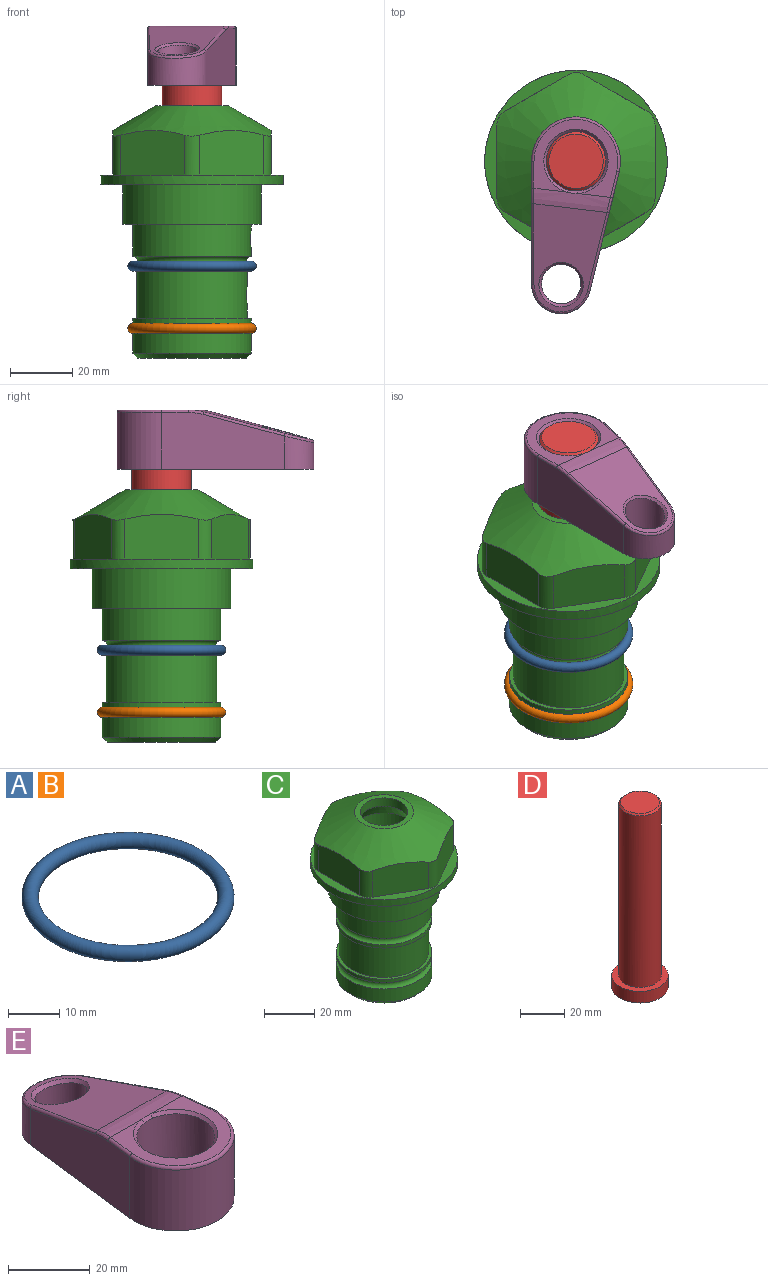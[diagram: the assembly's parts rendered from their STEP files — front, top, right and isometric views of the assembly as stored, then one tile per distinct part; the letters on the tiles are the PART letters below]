
ASSEMBLY  parts=5 mates=4
PART A: 1 faces, bbox 44.7x44.7x3.2 mm
  f0: torus R=19.05mm, axis (0,0,1), area 1193.9mm2
PART B: same geometry as A
PART C: 36 faces, bbox 58.7x58.7x81 mm
  f0: cylinder r=17.78mm len=35.56mm, axis (0,0,1), area 1670.8mm2, adj f23,f24,f31
  f1: cylinder r=19.05mm len=38.1mm, axis (0,0,1), area 1191.9mm2, adj f26,f27,f30
  f2: plane 58.66x58.66mm, normal (0,0,-1), area 1150.6mm2, adj f3,f28
  f3: cylinder r=29.33mm len=58.66mm, axis (0,0,-1), area 585.1mm2, adj f2,f4
  f4: plane 58.66x58.66mm, normal (0,0,1), area 475.9mm2, adj f3,f5,f6,f7,f8,f9,f10,f11
  f5: plane 20.32x14.34mm, normal (-0.5,0.87,0), area 324.4mm2, adj f4,f15,f16,f17
  f6: plane 20.32x14.34mm, normal (0.5,0.87,0), area 324.4mm2, adj f4,f14,f15,f17
  f7: plane 23.48x14.34mm, normal (1,0,0), area 324.4mm2, adj f4,f13,f14,f17
  f8: plane 20.32x14.34mm, normal (0.5,-0.87,0), area 324.4mm2, adj f4,f12,f13,f17
  f9: plane 20.32x14.34mm, normal (-0.5,-0.87,0), area 324.4mm2, adj f4,f11,f12,f17
  f10: plane 23.48x14.34mm, normal (-1,0,0), area 324.4mm2, adj f4,f11,f16,f17
  f11: cylinder r=5.08mm len=12.85mm, axis (0,0,-1), area 67.2mm2, adj f4,f9,f10,f17
  f12: cylinder r=5.08mm len=12.85mm, axis (0,0,-1), area 67.2mm2, adj f4,f8,f9,f17
  f13: cylinder r=5.08mm len=12.85mm, axis (0,0,-1), area 67.2mm2, adj f4,f7,f8,f17
  f14: cylinder r=5.08mm len=12.85mm, axis (0,0,-1), area 67.2mm2, adj f4,f6,f7,f17
  f15: cylinder r=5.08mm len=12.85mm, axis (0,0,-1), area 67.2mm2, adj f4,f5,f6,f17
  f16: cylinder r=5.08mm len=12.85mm, axis (0,0,-1), area 67.2mm2, adj f4,f5,f10,f17
  f17: cone r=11.73mm half-angle=60deg, axis (0,0,-1), area 2071.8mm2, adj f5,f6,f7,f8,f9,f10,f11,f12
  f18: plane 23.46x23.46mm, normal (0,0,1), area 147.4mm2, adj f17,f35
  f19: plane 34.93x34.93mm, normal (0,0,-1), area 958mm2, adj f29
  f20: cylinder r=19.05mm len=38.1mm, axis (0,0,1), area 760.1mm2, adj f21,f29
  f21: torus R=19.05mm, axis (0,0,1), area 565.3mm2, adj f20,f22
  f22: cylinder r=19.05mm len=38.1mm, axis (0,0,1), area 190mm2, adj f21,f23
  f23: plane 38.1x38.1mm, normal (0,0,1), area 146.9mm2, adj f0,f22
  f24: plane 38.1x38.1mm, normal (0,0,-1), area 146.9mm2, adj f0,f25
  f25: cylinder r=19.05mm len=38.1mm, axis (0,0,1), area 190mm2, adj f24,f26
  f26: torus R=19.05mm, axis (0,0,1), area 565.3mm2, adj f1,f25
  f27: plane 44.45x44.45mm, normal (0,0,-1), area 411.7mm2, adj f1,f28
  f28: cylinder r=22.23mm len=44.45mm, axis (0,0,1), area 1773.5mm2, adj f2,f27
  f29: cone r=19.05mm half-angle=45deg, axis (0,0,1), area 257.5mm2, adj f19,f20
  f30: cylinder r=3.17mm len=6.75mm, axis (-1,0,0), area 128mm2, adj f1,f33
  f31: cylinder r=3.17mm len=6.35mm, axis (-1,0,0), area 102.5mm2, adj f0,f33
  f32: plane 25.4x25.4mm, normal (0,0,1), area 506.7mm2, adj f33
  f33: cylinder r=12.7mm len=66.42mm, axis (0,0,-1), area 5236.2mm2, adj f30,f31,f32,f34
  f34: cone r=9.53mm half-angle=30deg, axis (0,0,-1), area 443.4mm2, adj f33,f35
  f35: cylinder r=9.53mm len=19.05mm, axis (0,0,-1), area 240.9mm2, adj f18,f34
PART D: 6 faces, bbox 25.4x25.4x101.6 mm
  f0: plane 17.46x17.46mm, normal (0,0,1), area 239.5mm2, adj f5
  f1: plane 25.4x25.4mm, normal (0,0,-1), area 506.7mm2, adj f2
  f2: cylinder r=12.7mm len=25.4mm, axis (0,0,1), area 506.7mm2, adj f1,f3
  f3: plane 25.4x25.4mm, normal (0,0,1), area 221.7mm2, adj f2,f4
  f4: cylinder r=9.53mm len=94.46mm, axis (0,0,1), area 5653mm2, adj f3,f5
  f5: cone r=8.73mm half-angle=45deg, axis (0,0,-1), area 64.4mm2, adj f0,f4
PART E: 31 faces, bbox 31.7x65.5x19.8 mm
  f0: plane 39.12x18.26mm, normal (0.99,0.12,0), area 612.2mm2, adj f1,f4,f7,f11,f13,f15
  f1: cylinder r=9.53mm len=18.91mm, axis (0,0,-1), area 296.1mm2, adj f0,f2,f7,f17
  f2: plane 39.12x18.26mm, normal (-0.99,0.12,0), area 612.2mm2, adj f1,f4,f7,f12,f14,f16
  f3: cylinder r=6.35mm len=12.7mm, axis (0,0,-1), area 362.4mm2, adj f7,f18
  f4: cylinder r=14.29mm len=28.58mm, axis (0,0,-1), area 882.2mm2, adj f0,f2,f7,f10
  f5: cylinder r=9.53mm len=19.05mm, axis (0,0,-1), area 1092.6mm2, adj f7,f19,f20
  f6: plane 26.99x23.69mm, normal (0,0,1), area 216.2mm2, adj f9,f10,f11,f12,f19
  f7: plane 63.5x28.58mm, normal (0,0,-1), area 661.8mm2, adj f0,f1,f2,f3,f4,f5,f22,f23
  f8: plane 33.52x23.6mm, normal (0,0.26,0.97), area 486mm2, adj f9,f15,f16,f17,f18
  f9: cylinder r=19.05mm len=24.72mm, axis (1,0,0), area 120.4mm2, adj f6,f8,f13,f14,f20
  f10: torus R=13.49mm, axis (0,0,1), area 59mm2, adj f4,f6,f11,f12
  f11: cylinder r=0.79mm len=8.67mm, axis (0.12,-0.99,0), area 10.8mm2, adj f0,f6,f10,f13
  f12: cylinder r=0.79mm len=8.67mm, axis (0.12,0.99,0), area 10.8mm2, adj f2,f6,f10,f14
  f13: bspline ~4.95x1.42mm, area 6.1mm2, adj f0,f9,f11,f15
  f14: bspline ~4.95x1.42mm, area 6.1mm2, adj f2,f9,f12,f16
  f15: cylinder r=0.79mm len=25.95mm, axis (0.12,-0.96,0.26), area 32.9mm2, adj f0,f8,f13,f17
  f16: cylinder r=0.79mm len=25.95mm, axis (0.12,0.96,-0.26), area 32.9mm2, adj f2,f8,f14,f17
  f17: bspline ~18.91x8.38mm, area 30mm2, adj f1,f8,f15,f16
  f18: bspline ~14.29x14.29mm, area 48.3mm2, adj f3,f8
  f19: cone r=9.53mm half-angle=45deg, axis (0,0,1), area 66.5mm2, adj f5,f6,f20
  f20: bspline ~3.22x0.96mm, area 3.5mm2, adj f5,f9,f19
  f21: plane 2.75x2.72mm, normal (0,0,-1), area 2.9mm2, adj f23,f25,f28
  f22: plane 23.05x15.88mm, normal (-0.99,-0.12,0), area 323.6mm2, adj f7,f25,f26,f27,f28,f29
  f23: plane 23.05x15.88mm, normal (0.99,-0.12,0), area 323.6mm2, adj f7,f21,f25,f27,f28,f30
  f24: cylinder r=9.53mm len=10.69mm, axis (0,0,-1), area 114.7mm2, adj f7,f27,f29,f30
  f25: cylinder r=12.7mm len=20.59mm, axis (0,0,-1), area 381.1mm2, adj f7,f21,f22,f23,f26,f28
  f26: plane 2.75x2.72mm, normal (0,0,-1), area 2.9mm2, adj f22,f25,f28
  f27: plane 19.72x18.37mm, normal (0,-0.26,-0.97), area 291.8mm2, adj f22,f23,f24,f28,f29,f30
  f28: cylinder r=15.88mm len=19.92mm, axis (1,0,0), area 54.8mm2, adj f21,f22,f23,f25,f26,f27
  f29: cylinder r=1.59mm len=11mm, axis (0,0,-1), area 34.7mm2, adj f7,f22,f24,f27
  f30: cylinder r=1.59mm len=11mm, axis (0,0,-1), area 34.7mm2, adj f7,f23,f24,f27
PLACE A t=(0,0,-1.59)mm
PLACE B t=(0,0,-21.59)mm
PLACE C at identity fixed
PLACE D rot(axis=(0,0,1),173.1deg) t=(0,0,-12.45)mm
PLACE E rot(axis=(0,0,1),173.1deg) t=(0,0,-12.45)mm
MATE fastened B.f0 <-> C.f0  axis (0,0,1) through (0,0,-46.1)mm
MATE fastened D.f2 <-> E.f4  axis (0,0,1) through (0,0,51.05)mm
MATE fastened A.f0 <-> C.f0  axis (0,0,1) through (0,0,-26.1)mm
MATE cylindrical D.f2 <-> C.f0  axis (0,0,-1) through (0,0,-50.55)mm
